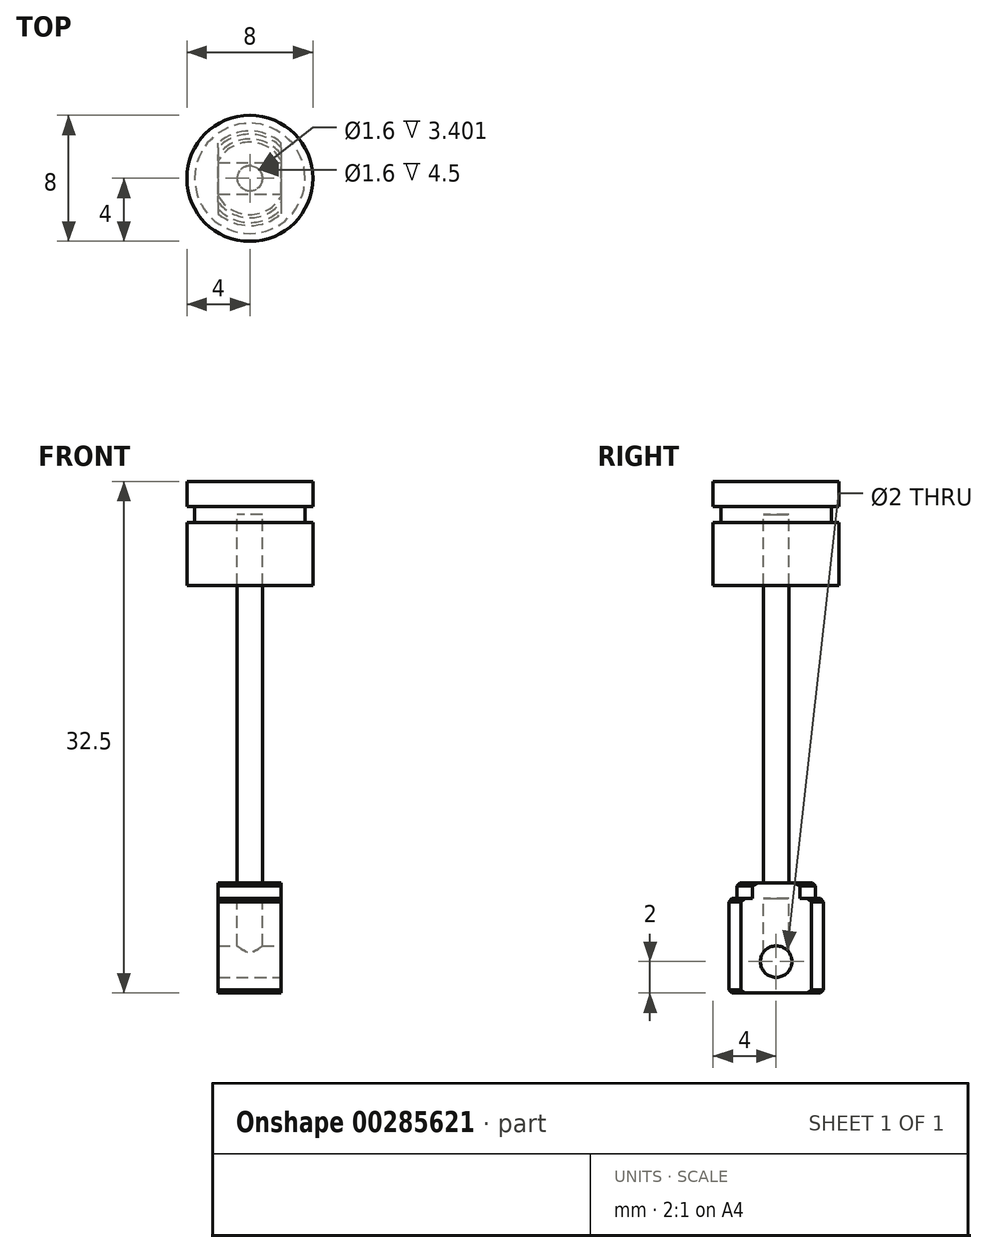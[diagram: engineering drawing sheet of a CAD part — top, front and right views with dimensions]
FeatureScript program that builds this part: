
annotation { "Feature Type Name" : "Feature", "Feature Type Description" : "" }
export const myFeature = defineFeature(function(context is Context, id is Id, definition is map)
    precondition{}
    {
        {
            var Q0;
            Q0=qCreatedBy(makeId("Front.planeOp"),FACE);
            var sketch = newSketch(context, id + "F0", { "sketchPlane" : qUnion([Q0])});
            skLineSegment(sketch, "E0", {"start": v(0, 19.03) * mm, "end": v(0, -16.97) * mm, "construction": true});
            skLineSegment(sketch, "E1", {"start": v(0, 32.5) * mm, "end": v(4, 32.5) * mm});
            skLineSegment(sketch, "E2", {"start": v(4, 32.5) * mm, "end": v(4, 30.9) * mm});
            skLineSegment(sketch, "E3", {"start": v(4, 30.9) * mm, "end": v(3.5, 30.9) * mm});
            skLineSegment(sketch, "E4", {"start": v(3.5, 30.9) * mm, "end": v(3.5, 29.9) * mm});
            skLineSegment(sketch, "E5", {"start": v(3.5, 29.9) * mm, "end": v(4, 29.9) * mm});
            skLineSegment(sketch, "E6", {"start": v(4, 29.9) * mm, "end": v(4, 25.9) * mm});
            skLineSegment(sketch, "E7", {"start": v(0, 32.5) * mm, "end": v(0, 30.4) * mm});
            skLineSegment(sketch, "E8", {"start": v(0, 30.4) * mm, "end": v(0.8, 30.4) * mm});
            skLineSegment(sketch, "E9", {"start": v(0.8, 30.4) * mm, "end": v(0.8, 25.9) * mm});
            skLineSegment(sketch, "E10", {"start": v(0.8, 25.9) * mm, "end": v(4, 25.9) * mm});
            skSolve(sketch);
        }
        {
            var Q0;
            Q0 = qSketchRegion(id + "F0", true);
            var Q1;
            Q1=sQuery(id+"F0.wireOp",EDGE,"E0");
            revolve(context, id + "F1", {"entities" : qUnion([Q0]), "axis" : qUnion([Q1]), "revolveType" : RevolveType.FULL});
        }
        {
            var Q0;
            Q0=makeQuery(id+"F1.opRevolve","SWEPT_FACE",FACE,{"disambiguationData":[OSD([sQuery(id+"F0.wireOp",EDGE,"E10")])]});
            var sketch = newSketch(context, id + "F2", { "sketchPlane" : qUnion([Q0])});
            skCircle(sketch, "E11", {"center": v(0, 0) * mm, "radius": 0.8 * mm});
            skSolve(sketch);
        }
        {
            var Q0;
            Q0 = qSketchRegion(id + "F2", true);
            extrude(context, id + "F3", {"entities" : qUnion([Q0]), "depth" : 22 * mm, "hasSecondDirection" : true, "secondDirectionOppositeDirection" : true, "secondDirectionDepth" : 4 * mm});
        }
        {
            var Q0;
            Q0=qCreatedBy(makeId("Top.planeOp"),FACE);
            var sketch = newSketch(context, id + "F4", { "sketchPlane" : qUnion([Q0])});
            skLineSegment(sketch, "E12", {"start": v(0, 7.11) * mm, "end": v(0, -8.1) * mm, "construction": true});
            skLineSegment(sketch, "E13", {"start": v(2, 2.24) * mm, "end": v(2, -2.24) * mm});
            skLineSegment(sketch, "E14", {"start": v(-2, 2.24) * mm, "end": v(-2, -2.24) * mm});
            skArc(sketch, "E15", {"start": v(-2, 2.24) * mm, "mid": v(0, 3) * mm, "end": v(2, 2.24) * mm});
            skArc(sketch, "E16", {"start": v(-2, -2.24) * mm, "mid": v(0, -3) * mm, "end": v(2, -2.24) * mm});
            skLineSegment(sketch, "E17", {"start": v(3.17, 0) * mm, "end": v(-3.56, 0) * mm, "construction": true});
            skSolve(sketch);
        }
        {
            var Q0;
            Q0 = qSketchRegion(id + "F4", true);
            extrude(context, id + "F5", {"entities" : qUnion([Q0]), "depth" : 6 * mm});
        }
        {
            var Q0;
            Q0=makeQuery(id+"F5.opExtrude","CAP_FACE",FACE,{"disambiguationData":[OSD([sQuery(id+"F4.wireOp",EDGE,"E13"),sQuery(id+"F4.wireOp",EDGE,"E14"),sQuery(id+"F4.wireOp",EDGE,"E15"),sQuery(id+"F4.wireOp",EDGE,"E16")])],"isStart":false});
            var sketch = newSketch(context, id + "F6", { "sketchPlane" : qUnion([Q0])});
            skCircle(sketch, "E18", {"center": v(0, 0) * mm, "radius": 0.8 * mm});
            skArc(sketch, "E19", {"start": v(-2, 1.5) * mm, "mid": v(0, 2.5) * mm, "end": v(2, 1.5) * mm});
            skArc(sketch, "E20", {"start": v(-2, -1.5) * mm, "mid": v(0, -2.5) * mm, "end": v(2, -1.5) * mm});
            skLineSegment(sketch, "E21", {"start": v(-2, 1.5) * mm, "end": v(-2, -1.5) * mm});
            skLineSegment(sketch, "E22", {"start": v(2, 1.5) * mm, "end": v(2, -1.5) * mm});
            skSolve(sketch);
        }
        {
            var Q0;
            Q0=makeQuery(id+"F6.imprint","IMPRINT",FACE,{"disambiguationData":[TD([[makeQuery(id+"F6.imprint","IMPRINT",EDGE,{"derivedFrom":sQuery(id+"F6.wireOp",EDGE,"E18")}),1.0]])]});
            extrude(context, id + "F7", {"entities" : qUnion([Q0]), "operationType" : NewBodyOperationType.REMOVE, "oppositeDirection" : true, "depth" : 4 * mm});
        }
        {
            var Q0;
            Q0=makeQuery(id+"F6.imprint","IMPRINT",FACE,{"disambiguationData":[TD([[makeQuery(id+"F6.imprint","IMPRINT",EDGE,{"derivedFrom":sQuery(id+"F6.wireOp",EDGE,"E18")}),-1.0]])]});
            extrude(context, id + "F8", {"entities" : qUnion([Q0]), "operationType" : NewBodyOperationType.ADD, "depth" : 1 * mm});
        }
        {
            var Q0;
            Q0=makeQuery(id+"F5.opExtrude","CAP_EDGE",EDGE,{"disambiguationData":[OSD([sQuery(id+"F4.wireOp",EDGE,"E16")])],"isStart":false});
            var Q1;
            Q1=makeQuery(id+"F8.opExtrude","CAP_EDGE",EDGE,{"disambiguationData":[OSD([sQuery(id+"F6.wireOp",EDGE,"E20")])],"isStart":false});
            var Q2;
            Q2=makeQuery(id+"F5.opExtrude","CAP_EDGE",EDGE,{"disambiguationData":[OSD([sQuery(id+"F4.wireOp",EDGE,"E15")])],"isStart":false});
            var Q3;
            Q3=makeQuery(id+"F8.opExtrude","CAP_EDGE",EDGE,{"disambiguationData":[OSD([sQuery(id+"F6.wireOp",EDGE,"E19")])],"isStart":false});
            var Q4;
            Q4=makeQuery(id+"F5.opExtrude","CAP_EDGE",EDGE,{"disambiguationData":[OSD([sQuery(id+"F4.wireOp",EDGE,"E16")])],"isStart":true});
            var Q5;
            Q5=makeQuery(id+"F5.opExtrude","CAP_EDGE",EDGE,{"disambiguationData":[OSD([sQuery(id+"F4.wireOp",EDGE,"E15")])],"isStart":true});
            chamfer(context, id + "F9", {"entities" : qUnion([Q0, Q1, Q2, Q3, Q4, Q5]), "width" : .2 * mm, "tangentPropagation" : true});
        }
        {
            var Q0;
            Q0=makeQuery(id+"F8.boolean.opBoolean","MERGE",FACE,{"derivedFrom":[makeQuery(id+"F5.opExtrude","SWEPT_FACE",FACE,{"disambiguationData":[OSD([sQuery(id+"F4.wireOp",EDGE,"E13")])]}),makeQuery(id+"F8.opExtrude","SWEPT_FACE",FACE,{"disambiguationData":[OSD([sQuery(id+"F6.wireOp",EDGE,"E22")])]})]});
            var sketch = newSketch(context, id + "F10", { "sketchPlane" : qUnion([Q0])});
            skLineSegment(sketch, "E23", {"start": v(0, 0) * mm, "end": v(0, 3.28) * mm, "construction": true});
            skCircle(sketch, "E24", {"center": v(0, 2) * mm, "radius": 1 * mm});
            skSolve(sketch);
        }
        {
            var Q0;
            Q0=makeQuery(id+"F10.imprint","IMPRINT",FACE,{"disambiguationData":[TD([[makeQuery(id+"F10.imprint","IMPRINT",EDGE,{"derivedFrom":sQuery(id+"F10.wireOp",EDGE,"E24")}),1.0]])]});
            extrude(context, id + "F11", {"entities" : qUnion([Q0]), "operationType" : NewBodyOperationType.REMOVE, "endBound" : BoundingType.THROUGH_ALL, "oppositeDirection" : true, "depth" : 25 * mm});
        }
    });
